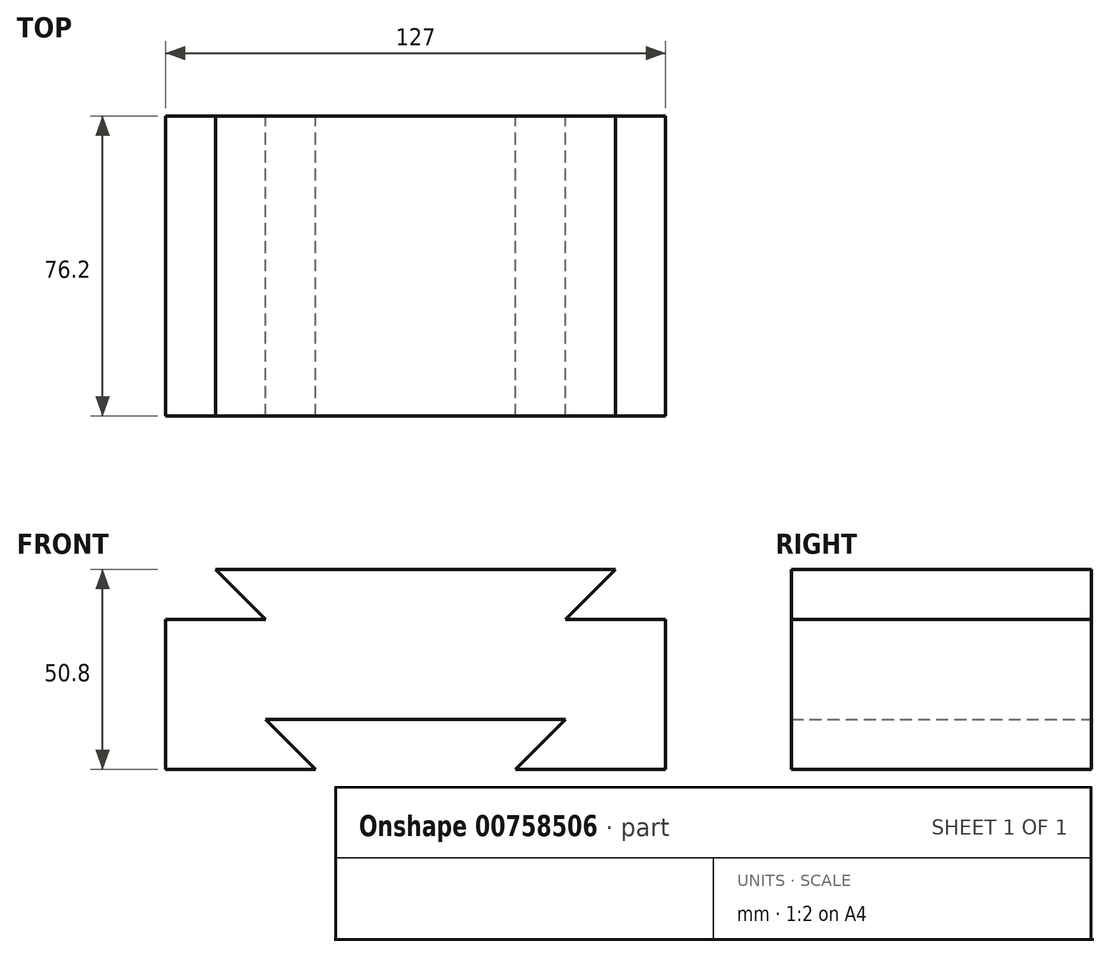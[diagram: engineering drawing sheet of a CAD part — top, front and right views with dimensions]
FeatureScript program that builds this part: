
annotation { "Feature Type Name" : "Feature", "Feature Type Description" : "" }
export const myFeature = defineFeature(function(context is Context, id is Id, definition is map)
    precondition{}
    {
        {
            var Q0;
            Q0=qCreatedBy(makeId("Front.planeOp"),FACE);
            var sketch = newSketch(context, id + "F0", { "sketchPlane" : qUnion([Q0])});
            skLineSegment(sketch, "E0", {"start": v(-58.4, 37.13) * mm, "end": v(43.2, 37.13) * mm});
            skLineSegment(sketch, "E1", {"start": v(-58.4, 37.13) * mm, "end": v(-45.7, 24.43) * mm});
            skLineSegment(sketch, "E2", {"start": v(43.2, 37.13) * mm, "end": v(30.5, 24.43) * mm});
            skLineSegment(sketch, "E3", {"start": v(30.5, 24.43) * mm, "end": v(55.9, 24.43) * mm});
            skLineSegment(sketch, "E4", {"start": v(-71.1, 24.43) * mm, "end": v(-45.7, 24.43) * mm});
            skLineSegment(sketch, "E5", {"start": v(55.9, 24.43) * mm, "end": v(55.9, -13.67) * mm});
            skLineSegment(sketch, "E6", {"start": v(55.9, -13.67) * mm, "end": v(17.8, -13.67) * mm});
            skLineSegment(sketch, "E7", {"start": v(-71.1, 24.43) * mm, "end": v(-71.1, -13.67) * mm});
            skLineSegment(sketch, "E8", {"start": v(-71.1, -13.67) * mm, "end": v(-33, -13.67) * mm});
            skLineSegment(sketch, "E9", {"start": v(-45.7, -0.97) * mm, "end": v(-33, -13.67) * mm});
            skLineSegment(sketch, "E10", {"start": v(30.5, -0.97) * mm, "end": v(17.8, -13.67) * mm});
            skLineSegment(sketch, "E11", {"start": v(-45.7, -0.97) * mm, "end": v(30.5, -0.97) * mm});
            skSolve(sketch);
        }
        {
            var Q0;
            Q0=makeQuery(id+"F0.imprint","IMPRINT",FACE,{"disambiguationData":[TD([[makeQuery(id+"F0.imprint","IMPRINT",EDGE,{"derivedFrom":sQuery(id+"F0.wireOp",EDGE,"E0")}),-1.0]])]});
            extrude(context, id + "F1", {"entities" : qUnion([Q0]), "depth" : 76.2 * mm, "offsetDistance" : 25.4 * mm});
        }
    });
